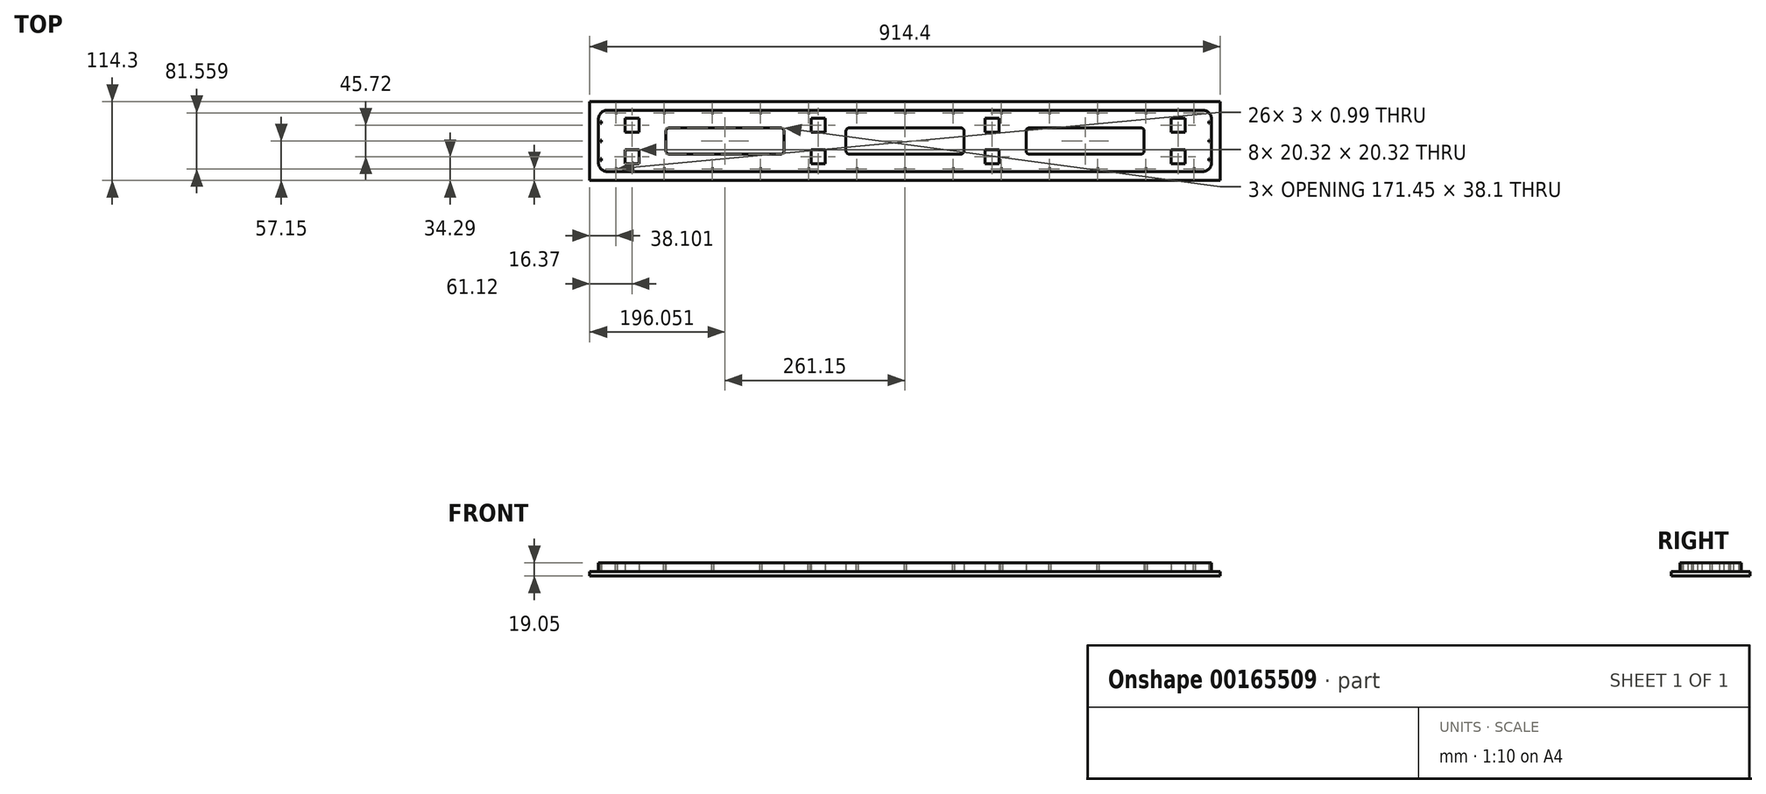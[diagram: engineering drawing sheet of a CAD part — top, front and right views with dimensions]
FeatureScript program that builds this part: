
annotation { "Feature Type Name" : "Feature", "Feature Type Description" : "" }
export const myFeature = defineFeature(function(context is Context, id is Id, definition is map)
    precondition{}
    {
        {
            var Q0;
            Q0=qCreatedBy(makeId("Top.planeOp"),FACE);
            var sketch = newSketch(context, id + "F0", { "sketchPlane" : qUnion([Q0])});
            skLineSegment(sketch, "E0.bottom", {"start": v(0, 33.02) * mm, "end": v(20.32, 33.02) * mm});
            skLineSegment(sketch, "E0.top", {"start": v(0, 12.7) * mm, "end": v(20.32, 12.7) * mm});
            skLineSegment(sketch, "E0.left", {"start": v(0, 33.02) * mm, "end": v(0, 12.7) * mm});
            skLineSegment(sketch, "E0.right", {"start": v(20.32, 33.02) * mm, "end": v(20.32, 12.7) * mm});
            skLineSegment(sketch, "E1.bottom", {"start": v(269.88, 12.7) * mm, "end": v(290.2, 12.7) * mm});
            skLineSegment(sketch, "E1.top", {"start": v(269.88, 33.02) * mm, "end": v(290.2, 33.02) * mm});
            skLineSegment(sketch, "E1.left", {"start": v(269.88, 12.7) * mm, "end": v(269.88, 33.02) * mm});
            skLineSegment(sketch, "E1.right", {"start": v(290.2, 12.7) * mm, "end": v(290.2, 33.02) * mm});
            skLineSegment(sketch, "E2.bottom", {"start": v(522.3, 12.7) * mm, "end": v(542.62, 12.7) * mm});
            skLineSegment(sketch, "E2.top", {"start": v(522.3, 33.02) * mm, "end": v(542.62, 33.02) * mm});
            skLineSegment(sketch, "E2.left", {"start": v(522.3, 12.7) * mm, "end": v(522.3, 33.02) * mm});
            skLineSegment(sketch, "E2.right", {"start": v(542.62, 12.7) * mm, "end": v(542.62, 33.02) * mm});
            skLineSegment(sketch, "E3.bottom", {"start": v(792.16, 12.7) * mm, "end": v(812.48, 12.7) * mm});
            skLineSegment(sketch, "E3.top", {"start": v(792.16, 33.02) * mm, "end": v(812.48, 33.02) * mm});
            skLineSegment(sketch, "E3.left", {"start": v(792.16, 12.7) * mm, "end": v(792.16, 33.02) * mm});
            skLineSegment(sketch, "E3.right", {"start": v(812.48, 12.7) * mm, "end": v(812.48, 33.02) * mm});
            skLineSegment(sketch, "E4.MirrorCS", {"start": v(0, -33.02) * mm, "end": v(0, -12.7) * mm});
            skLineSegment(sketch, "E5.MirrorCS", {"start": v(269.88, -12.7) * mm, "end": v(290.2, -12.7) * mm});
            skLineSegment(sketch, "E6.MirrorCS", {"start": v(0, -33.02) * mm, "end": v(20.32, -33.02) * mm});
            skLineSegment(sketch, "E7.MirrorCS", {"start": v(792.16, -33.02) * mm, "end": v(812.48, -33.02) * mm});
            skLineSegment(sketch, "E8.MirrorCS", {"start": v(792.16, -12.7) * mm, "end": v(792.16, -33.02) * mm});
            skLineSegment(sketch, "E9.MirrorCS", {"start": v(812.48, -12.7) * mm, "end": v(812.48, -33.02) * mm});
            skLineSegment(sketch, "E10.MirrorCS", {"start": v(20.32, -33.02) * mm, "end": v(20.32, -12.7) * mm});
            skLineSegment(sketch, "E11.MirrorCS", {"start": v(269.88, -33.02) * mm, "end": v(290.2, -33.02) * mm});
            skLineSegment(sketch, "E12.MirrorCS", {"start": v(269.88, -12.7) * mm, "end": v(269.88, -33.02) * mm});
            skLineSegment(sketch, "E13.MirrorCS", {"start": v(290.2, -12.7) * mm, "end": v(290.2, -33.02) * mm});
            skLineSegment(sketch, "E14.MirrorCS", {"start": v(522.3, -12.7) * mm, "end": v(542.62, -12.7) * mm});
            skLineSegment(sketch, "E15.MirrorCS", {"start": v(522.3, -33.02) * mm, "end": v(542.62, -33.02) * mm});
            skLineSegment(sketch, "E16.MirrorCS", {"start": v(522.3, -12.7) * mm, "end": v(522.3, -33.02) * mm});
            skLineSegment(sketch, "E17.MirrorCS", {"start": v(542.62, -12.7) * mm, "end": v(542.62, -33.02) * mm});
            skLineSegment(sketch, "E18.MirrorCS", {"start": v(792.16, -12.7) * mm, "end": v(812.48, -12.7) * mm});
            skLineSegment(sketch, "E19.MirrorCS", {"start": v(0, -12.7) * mm, "end": v(20.32, -12.7) * mm});
            skLineSegment(sketch, "E20", {"start": v(0, 0) * mm, "end": v(812.48, 0) * mm, "construction": true});
            skLineSegment(sketch, "E21.bottom", {"start": v(-38.26, -44.45) * mm, "end": v(850.74, -44.45) * mm});
            skLineSegment(sketch, "E21.top", {"start": v(-38.26, 44.45) * mm, "end": v(850.74, 44.45) * mm});
            skLineSegment(sketch, "E21.left", {"start": v(-38.26, -44.45) * mm, "end": v(-38.26, 44.45) * mm});
            skLineSegment(sketch, "E21.right", {"start": v(850.74, -44.45) * mm, "end": v(850.74, 44.45) * mm});
            skPoint(sketch, "E21.middle", {"position": v(406.24, 0) * mm});
            skLineSegment(sketch, "E22.bottom", {"start": v(407.74, 40.28) * mm, "end": v(404.74, 40.28) * mm});
            skLineSegment(sketch, "E22.top", {"start": v(407.74, 41.28) * mm, "end": v(404.74, 41.28) * mm});
            skLineSegment(sketch, "E22.left", {"start": v(407.74, 40.28) * mm, "end": v(407.74, 41.28) * mm});
            skLineSegment(sketch, "E22.right", {"start": v(404.74, 40.28) * mm, "end": v(404.74, 41.28) * mm});
            skPoint(sketch, "E22.middle", {"position": v(406.24, 40.78) * mm});
            skLineSegment(sketch, "E23.1.0.0", {"start": v(477.59, 41.28) * mm, "end": v(474.6, 41.28) * mm});
            skLineSegment(sketch, "E23.1.0.1", {"start": v(474.6, 40.28) * mm, "end": v(474.6, 41.28) * mm});
            skLineSegment(sketch, "E23.1.0.2", {"start": v(477.59, 40.28) * mm, "end": v(474.6, 40.28) * mm});
            skLineSegment(sketch, "E23.1.0.3", {"start": v(477.59, 40.28) * mm, "end": v(477.59, 41.28) * mm});
            skLineSegment(sketch, "E23.2.0.0", {"start": v(547.44, 41.28) * mm, "end": v(544.44, 41.28) * mm});
            skLineSegment(sketch, "E23.2.0.1", {"start": v(544.44, 40.28) * mm, "end": v(544.44, 41.28) * mm});
            skLineSegment(sketch, "E23.2.0.2", {"start": v(547.44, 40.28) * mm, "end": v(544.44, 40.28) * mm});
            skLineSegment(sketch, "E23.2.0.3", {"start": v(547.44, 40.28) * mm, "end": v(547.44, 41.28) * mm});
            skLineSegment(sketch, "E23.3.0.0", {"start": v(617.29, 41.28) * mm, "end": v(614.3, 41.28) * mm});
            skLineSegment(sketch, "E23.3.0.1", {"start": v(614.3, 40.28) * mm, "end": v(614.3, 41.28) * mm});
            skLineSegment(sketch, "E23.3.0.2", {"start": v(617.29, 40.28) * mm, "end": v(614.3, 40.28) * mm});
            skLineSegment(sketch, "E23.3.0.3", {"start": v(617.29, 40.28) * mm, "end": v(617.29, 41.28) * mm});
            skLineSegment(sketch, "E23.4.0.0", {"start": v(687.14, 41.28) * mm, "end": v(684.14, 41.28) * mm});
            skLineSegment(sketch, "E23.4.0.1", {"start": v(684.14, 40.28) * mm, "end": v(684.14, 41.28) * mm});
            skLineSegment(sketch, "E23.4.0.2", {"start": v(687.14, 40.28) * mm, "end": v(684.14, 40.28) * mm});
            skLineSegment(sketch, "E23.4.0.3", {"start": v(687.14, 40.28) * mm, "end": v(687.14, 41.28) * mm});
            skLineSegment(sketch, "E23.5.0.0", {"start": v(756.99, 41.28) * mm, "end": v(754, 41.28) * mm});
            skLineSegment(sketch, "E23.5.0.1", {"start": v(754, 40.28) * mm, "end": v(754, 41.28) * mm});
            skLineSegment(sketch, "E23.5.0.2", {"start": v(756.99, 40.28) * mm, "end": v(754, 40.28) * mm});
            skLineSegment(sketch, "E23.5.0.3", {"start": v(756.99, 40.28) * mm, "end": v(756.99, 41.28) * mm});
            skLineSegment(sketch, "E23.6.0.0", {"start": v(826.84, 41.28) * mm, "end": v(823.84, 41.28) * mm});
            skLineSegment(sketch, "E23.6.0.1", {"start": v(823.84, 40.28) * mm, "end": v(823.84, 41.28) * mm});
            skLineSegment(sketch, "E23.6.0.2", {"start": v(826.84, 40.28) * mm, "end": v(823.84, 40.28) * mm});
            skLineSegment(sketch, "E23.6.0.3", {"start": v(826.84, 40.28) * mm, "end": v(826.84, 41.28) * mm});
            skLineSegment(sketch, "E23.direction1", {"start": v(404.74, 41.28) * mm, "end": v(474.6, 41.28) * mm, "construction": true});
            skLineSegment(sketch, "E24", {"start": v(406.24, 44.45) * mm, "end": v(406.24, -44.45) * mm, "construction": true});
            skLineSegment(sketch, "E25.MirrorCS", {"start": v(58.49, 40.28) * mm, "end": v(58.49, 41.28) * mm});
            skLineSegment(sketch, "E26.MirrorCS", {"start": v(337.89, 40.28) * mm, "end": v(337.89, 41.28) * mm});
            skLineSegment(sketch, "E27.MirrorCS", {"start": v(334.9, 40.28) * mm, "end": v(337.89, 40.28) * mm});
            skLineSegment(sketch, "E28.MirrorCS", {"start": v(195.2, 40.28) * mm, "end": v(198.19, 40.28) * mm});
            skLineSegment(sketch, "E29.MirrorCS", {"start": v(55.5, 40.28) * mm, "end": v(58.49, 40.28) * mm});
            skLineSegment(sketch, "E30.MirrorCS", {"start": v(-14.36, 41.28) * mm, "end": v(-11.36, 41.28) * mm});
            skLineSegment(sketch, "E31.MirrorCS", {"start": v(195.2, 40.28) * mm, "end": v(195.2, 41.28) * mm});
            skLineSegment(sketch, "E32.MirrorCS", {"start": v(265.04, 41.28) * mm, "end": v(268.04, 41.28) * mm});
            skLineSegment(sketch, "E33.MirrorCS", {"start": v(55.5, 40.28) * mm, "end": v(55.5, 41.28) * mm});
            skLineSegment(sketch, "E34.MirrorCS", {"start": v(334.9, 40.28) * mm, "end": v(334.9, 41.28) * mm});
            skLineSegment(sketch, "E35.MirrorCS", {"start": v(-11.36, 40.28) * mm, "end": v(-11.36, 41.28) * mm});
            skLineSegment(sketch, "E36.MirrorCS", {"start": v(125.34, 41.28) * mm, "end": v(128.34, 41.28) * mm});
            skLineSegment(sketch, "E37.MirrorCS", {"start": v(268.04, 40.28) * mm, "end": v(268.04, 41.28) * mm});
            skLineSegment(sketch, "E38.MirrorCS", {"start": v(-14.36, 40.28) * mm, "end": v(-11.36, 40.28) * mm});
            skLineSegment(sketch, "E39.MirrorCS", {"start": v(265.04, 40.28) * mm, "end": v(268.04, 40.28) * mm});
            skLineSegment(sketch, "E40.MirrorCS", {"start": v(128.34, 40.28) * mm, "end": v(128.34, 41.28) * mm});
            skLineSegment(sketch, "E41.MirrorCS", {"start": v(125.34, 40.28) * mm, "end": v(128.34, 40.28) * mm});
            skLineSegment(sketch, "E42.MirrorCS", {"start": v(-14.36, 40.28) * mm, "end": v(-14.36, 41.28) * mm});
            skLineSegment(sketch, "E43.MirrorCS", {"start": v(265.04, 40.28) * mm, "end": v(265.04, 41.28) * mm});
            skLineSegment(sketch, "E44.MirrorCS", {"start": v(125.34, 40.28) * mm, "end": v(125.34, 41.28) * mm});
            skLineSegment(sketch, "E45.MirrorCS", {"start": v(195.2, 41.28) * mm, "end": v(198.19, 41.28) * mm});
            skLineSegment(sketch, "E46.MirrorCS", {"start": v(55.5, 41.28) * mm, "end": v(58.49, 41.28) * mm});
            skLineSegment(sketch, "E47.MirrorCS", {"start": v(334.9, 41.28) * mm, "end": v(337.89, 41.28) * mm});
            skLineSegment(sketch, "E48.MirrorCS", {"start": v(198.19, 40.28) * mm, "end": v(198.19, 41.28) * mm});
            skLineSegment(sketch, "E49.MirrorCS", {"start": v(404.74, -40.28) * mm, "end": v(404.74, -41.28) * mm});
            skLineSegment(sketch, "E50.MirrorCS", {"start": v(407.74, -40.28) * mm, "end": v(407.74, -41.28) * mm});
            skLineSegment(sketch, "E51.MirrorCS", {"start": v(407.74, -40.28) * mm, "end": v(404.74, -40.28) * mm});
            skLineSegment(sketch, "E52.MirrorCS", {"start": v(407.74, -41.28) * mm, "end": v(404.74, -41.28) * mm});
            skLineSegment(sketch, "E53.MirrorCS", {"start": v(477.59, -40.28) * mm, "end": v(477.59, -41.28) * mm});
            skLineSegment(sketch, "E54.MirrorCS", {"start": v(477.59, -40.28) * mm, "end": v(474.6, -40.28) * mm});
            skLineSegment(sketch, "E55.MirrorCS", {"start": v(474.6, -40.28) * mm, "end": v(474.6, -41.28) * mm});
            skLineSegment(sketch, "E56.MirrorCS", {"start": v(477.59, -41.28) * mm, "end": v(474.6, -41.28) * mm});
            skLineSegment(sketch, "E57.MirrorCS", {"start": v(58.49, -40.28) * mm, "end": v(58.49, -41.28) * mm});
            skLineSegment(sketch, "E58.MirrorCS", {"start": v(-14.36, -40.28) * mm, "end": v(-14.36, -41.28) * mm});
            skLineSegment(sketch, "E59.MirrorCS", {"start": v(128.34, -40.28) * mm, "end": v(128.34, -41.28) * mm});
            skLineSegment(sketch, "E60.MirrorCS", {"start": v(265.04, -40.28) * mm, "end": v(268.04, -40.28) * mm});
            skLineSegment(sketch, "E61.MirrorCS", {"start": v(-14.36, -40.28) * mm, "end": v(-11.36, -40.28) * mm});
            skLineSegment(sketch, "E62.MirrorCS", {"start": v(268.04, -40.28) * mm, "end": v(268.04, -41.28) * mm});
            skLineSegment(sketch, "E63.MirrorCS", {"start": v(125.34, -41.28) * mm, "end": v(128.34, -41.28) * mm});
            skLineSegment(sketch, "E64.MirrorCS", {"start": v(334.9, -40.28) * mm, "end": v(334.9, -41.28) * mm});
            skLineSegment(sketch, "E65.MirrorCS", {"start": v(-11.36, -40.28) * mm, "end": v(-11.36, -41.28) * mm});
            skLineSegment(sketch, "E66.MirrorCS", {"start": v(55.5, -40.28) * mm, "end": v(55.5, -41.28) * mm});
            skLineSegment(sketch, "E67.MirrorCS", {"start": v(265.04, -41.28) * mm, "end": v(268.04, -41.28) * mm});
            skLineSegment(sketch, "E68.MirrorCS", {"start": v(198.19, -40.28) * mm, "end": v(198.19, -41.28) * mm});
            skLineSegment(sketch, "E69.MirrorCS", {"start": v(195.2, -40.28) * mm, "end": v(195.2, -41.28) * mm});
            skLineSegment(sketch, "E70.MirrorCS", {"start": v(334.9, -41.28) * mm, "end": v(337.89, -41.28) * mm});
            skLineSegment(sketch, "E71.MirrorCS", {"start": v(-14.36, -41.28) * mm, "end": v(-11.36, -41.28) * mm});
            skLineSegment(sketch, "E72.MirrorCS", {"start": v(55.5, -41.28) * mm, "end": v(58.49, -41.28) * mm});
            skLineSegment(sketch, "E73.MirrorCS", {"start": v(55.5, -40.28) * mm, "end": v(58.49, -40.28) * mm});
            skLineSegment(sketch, "E74.MirrorCS", {"start": v(195.2, -41.28) * mm, "end": v(198.19, -41.28) * mm});
            skLineSegment(sketch, "E75.MirrorCS", {"start": v(125.34, -40.28) * mm, "end": v(125.34, -41.28) * mm});
            skLineSegment(sketch, "E76.MirrorCS", {"start": v(334.9, -40.28) * mm, "end": v(337.89, -40.28) * mm});
            skLineSegment(sketch, "E77.MirrorCS", {"start": v(195.2, -40.28) * mm, "end": v(198.19, -40.28) * mm});
            skLineSegment(sketch, "E78.MirrorCS", {"start": v(337.89, -40.28) * mm, "end": v(337.89, -41.28) * mm});
            skLineSegment(sketch, "E79.MirrorCS", {"start": v(125.34, -40.28) * mm, "end": v(128.34, -40.28) * mm});
            skLineSegment(sketch, "E80.MirrorCS", {"start": v(265.04, -40.28) * mm, "end": v(265.04, -41.28) * mm});
            skLineSegment(sketch, "E81.MirrorCS", {"start": v(404.74, -41.28) * mm, "end": v(474.6, -41.28) * mm, "construction": true});
            skPoint(sketch, "E82.MirrorP", {"position": v(406.24, -40.78) * mm});
            skLineSegment(sketch, "E83.MirrorCS", {"start": v(617.29, -40.28) * mm, "end": v(614.3, -40.28) * mm});
            skLineSegment(sketch, "E84.MirrorCS", {"start": v(617.29, -40.28) * mm, "end": v(617.29, -41.28) * mm});
            skLineSegment(sketch, "E85.MirrorCS", {"start": v(687.14, -41.28) * mm, "end": v(684.14, -41.28) * mm});
            skLineSegment(sketch, "E86.MirrorCS", {"start": v(684.14, -40.28) * mm, "end": v(684.14, -41.28) * mm});
            skLineSegment(sketch, "E87.MirrorCS", {"start": v(687.14, -40.28) * mm, "end": v(684.14, -40.28) * mm});
            skLineSegment(sketch, "E88.MirrorCS", {"start": v(687.14, -40.28) * mm, "end": v(687.14, -41.28) * mm});
            skLineSegment(sketch, "E89.MirrorCS", {"start": v(756.99, -41.28) * mm, "end": v(754, -41.28) * mm});
            skLineSegment(sketch, "E90.MirrorCS", {"start": v(754, -40.28) * mm, "end": v(754, -41.28) * mm});
            skLineSegment(sketch, "E91.MirrorCS", {"start": v(756.99, -40.28) * mm, "end": v(754, -40.28) * mm});
            skLineSegment(sketch, "E92.MirrorCS", {"start": v(826.84, -41.28) * mm, "end": v(823.84, -41.28) * mm});
            skLineSegment(sketch, "E93.MirrorCS", {"start": v(547.44, -41.28) * mm, "end": v(544.44, -41.28) * mm});
            skLineSegment(sketch, "E94.MirrorCS", {"start": v(614.3, -40.28) * mm, "end": v(614.3, -41.28) * mm});
            skLineSegment(sketch, "E95.MirrorCS", {"start": v(547.44, -40.28) * mm, "end": v(547.44, -41.28) * mm});
            skLineSegment(sketch, "E96.MirrorCS", {"start": v(826.84, -40.28) * mm, "end": v(826.84, -41.28) * mm});
            skLineSegment(sketch, "E97.MirrorCS", {"start": v(756.99, -40.28) * mm, "end": v(756.99, -41.28) * mm});
            skLineSegment(sketch, "E98.MirrorCS", {"start": v(823.84, -40.28) * mm, "end": v(823.84, -41.28) * mm});
            skLineSegment(sketch, "E99.MirrorCS", {"start": v(826.84, -40.28) * mm, "end": v(823.84, -40.28) * mm});
            skLineSegment(sketch, "E100.MirrorCS", {"start": v(617.29, -41.28) * mm, "end": v(614.3, -41.28) * mm});
            skLineSegment(sketch, "E101.MirrorCS", {"start": v(547.44, -40.28) * mm, "end": v(544.44, -40.28) * mm});
            skLineSegment(sketch, "E102.MirrorCS", {"start": v(544.44, -40.28) * mm, "end": v(544.44, -41.28) * mm});
            skLineSegment(sketch, "E103.bottom", {"start": v(847.57, -1.5) * mm, "end": v(846.58, -1.5) * mm});
            skLineSegment(sketch, "E103.top", {"start": v(847.57, 1.5) * mm, "end": v(846.58, 1.5) * mm});
            skLineSegment(sketch, "E103.left", {"start": v(847.57, -1.5) * mm, "end": v(847.57, 1.5) * mm});
            skLineSegment(sketch, "E103.right", {"start": v(846.58, -1.5) * mm, "end": v(846.58, 1.5) * mm});
            skPoint(sketch, "E103.middle", {"position": v(847.07, 0) * mm});
            skLineSegment(sketch, "E104.bottom", {"start": v(847.57, 25.49) * mm, "end": v(846.58, 25.49) * mm});
            skLineSegment(sketch, "E104.top", {"start": v(847.57, 28.49) * mm, "end": v(846.58, 28.49) * mm});
            skLineSegment(sketch, "E104.left", {"start": v(847.57, 25.49) * mm, "end": v(847.57, 28.49) * mm});
            skLineSegment(sketch, "E104.right", {"start": v(846.58, 25.49) * mm, "end": v(846.58, 28.49) * mm});
            skPoint(sketch, "E104.middle", {"position": v(847.07, 26.99) * mm});
            skLineSegment(sketch, "E105.MirrorCS", {"start": v(847.57, -28.49) * mm, "end": v(846.58, -28.49) * mm});
            skLineSegment(sketch, "E106.MirrorCS", {"start": v(847.57, -25.49) * mm, "end": v(846.58, -25.49) * mm});
            skLineSegment(sketch, "E107.MirrorCS", {"start": v(846.58, -25.49) * mm, "end": v(846.58, -28.49) * mm});
            skLineSegment(sketch, "E108.MirrorCS", {"start": v(847.57, -25.49) * mm, "end": v(847.57, -28.49) * mm});
            skPoint(sketch, "E109.MirrorP", {"position": v(847.07, -26.99) * mm});
            skLineSegment(sketch, "E110.MirrorCS", {"start": v(-35.08, 25.49) * mm, "end": v(-34.1, 25.49) * mm});
            skLineSegment(sketch, "E111.MirrorCS", {"start": v(-35.08, 28.49) * mm, "end": v(-34.1, 28.49) * mm});
            skLineSegment(sketch, "E112.MirrorCS", {"start": v(-35.08, -28.49) * mm, "end": v(-34.1, -28.49) * mm});
            skLineSegment(sketch, "E113.MirrorCS", {"start": v(-35.08, -25.49) * mm, "end": v(-34.1, -25.49) * mm});
            skLineSegment(sketch, "E114.MirrorCS", {"start": v(-35.08, -1.5) * mm, "end": v(-34.1, -1.5) * mm});
            skLineSegment(sketch, "E115.MirrorCS", {"start": v(-35.08, 1.5) * mm, "end": v(-34.1, 1.5) * mm});
            skLineSegment(sketch, "E116.MirrorCS", {"start": v(-34.1, -1.5) * mm, "end": v(-34.1, 1.5) * mm});
            skLineSegment(sketch, "E117.MirrorCS", {"start": v(-35.08, 25.49) * mm, "end": v(-35.08, 28.49) * mm});
            skLineSegment(sketch, "E118.MirrorCS", {"start": v(-34.1, 25.49) * mm, "end": v(-34.1, 28.49) * mm});
            skLineSegment(sketch, "E119.MirrorCS", {"start": v(-34.1, -25.49) * mm, "end": v(-34.1, -28.49) * mm});
            skLineSegment(sketch, "E120.MirrorCS", {"start": v(-35.08, -25.49) * mm, "end": v(-35.08, -28.49) * mm});
            skLineSegment(sketch, "E121.MirrorCS", {"start": v(-35.08, -1.5) * mm, "end": v(-35.08, 1.5) * mm});
            skPoint(sketch, "E122.MirrorP", {"position": v(-34.59, -26.99) * mm});
            skPoint(sketch, "E123.MirrorP", {"position": v(-34.59, 0) * mm});
            skPoint(sketch, "E124.MirrorP", {"position": v(-34.59, 26.99) * mm});
            skLineSegment(sketch, "E125.bottom", {"start": v(491.97, -19.05) * mm, "end": v(320.52, -19.05) * mm});
            skLineSegment(sketch, "E125.top", {"start": v(491.97, 19.05) * mm, "end": v(320.52, 19.05) * mm});
            skLineSegment(sketch, "E125.left", {"start": v(491.97, -19.05) * mm, "end": v(491.97, 19.05) * mm});
            skLineSegment(sketch, "E125.right", {"start": v(320.52, -19.05) * mm, "end": v(320.52, 19.05) * mm});
            skLineSegment(sketch, "E126", {"start": v(542.62, 12.7) * mm, "end": v(792.16, 12.7) * mm, "construction": true});
            skLineSegment(sketch, "E127.bottom", {"start": v(753.12, -19.05) * mm, "end": v(581.67, -19.05) * mm});
            skLineSegment(sketch, "E127.top", {"start": v(753.12, 19.05) * mm, "end": v(581.67, 19.05) * mm});
            skLineSegment(sketch, "E127.left", {"start": v(753.12, -19.05) * mm, "end": v(753.12, 19.05) * mm});
            skLineSegment(sketch, "E127.right", {"start": v(581.67, -19.05) * mm, "end": v(581.67, 19.05) * mm});
            skPoint(sketch, "E127.middle", {"position": v(667.4, 0) * mm});
            skPoint(sketch, "E127.middle.positionSnap0", {"position": v(667.4, 12.7) * mm});
            skPoint(sketch, "E127.centerSnap0", {"position": v(667.4, 12.7) * mm});
            skPoint(sketch, "E128.MirrorP", {"position": v(145.1, 12.7) * mm});
            skLineSegment(sketch, "E129.MirrorCS", {"start": v(59.37, 19.05) * mm, "end": v(230.82, 19.05) * mm});
            skPoint(sketch, "E130.MirrorP", {"position": v(145.1, 0) * mm});
            skLineSegment(sketch, "E131.MirrorCS", {"start": v(230.82, -19.05) * mm, "end": v(230.82, 19.05) * mm});
            skLineSegment(sketch, "E132.MirrorCS", {"start": v(59.37, -19.05) * mm, "end": v(230.82, -19.05) * mm});
            skLineSegment(sketch, "E133.MirrorCS", {"start": v(59.37, -19.05) * mm, "end": v(59.37, 19.05) * mm});
            skLineSegment(sketch, "E134.bottom", {"start": v(863.44, -57.15) * mm, "end": v(-50.96, -57.15) * mm, "construction": true});
            skLineSegment(sketch, "E134.top", {"start": v(863.44, 57.15) * mm, "end": v(-50.96, 57.15) * mm, "construction": true});
            skLineSegment(sketch, "E134.left", {"start": v(863.44, -57.15) * mm, "end": v(863.44, 57.15) * mm, "construction": true});
            skLineSegment(sketch, "E134.right", {"start": v(-50.96, -57.15) * mm, "end": v(-50.96, 57.15) * mm, "construction": true});
            skSolve(sketch);
        }
        {
            var Q0;
            Q0=qSketchRegion(id+"F0",true);
            extrude(context, id + "F1", {"entities" : qUnion([Q0]), "depth" : 12.7 * mm});
        }
        {
            var Q0;
            Q0=makeQuery(id+"F1.opExtrude","SWEPT_EDGE",EDGE,{"disambiguationData":[OSD([sQuery(id+"F0.wireOp",EDGE,"E21.top"),sQuery(id+"F0.wireOp",EDGE,"E21.right")])]});
            var Q1;
            Q1=makeQuery(id+"F1.opExtrude","SWEPT_EDGE",EDGE,{"disambiguationData":[OSD([sQuery(id+"F0.wireOp",EDGE,"E21.bottom"),sQuery(id+"F0.wireOp",EDGE,"E21.right")])]});
            var Q2;
            Q2=makeQuery(id+"F1.opExtrude","SWEPT_EDGE",EDGE,{"disambiguationData":[OSD([sQuery(id+"F0.wireOp",EDGE,"E21.top"),sQuery(id+"F0.wireOp",EDGE,"E21.left")])]});
            var Q3;
            Q3=makeQuery(id+"F1.opExtrude","SWEPT_EDGE",EDGE,{"disambiguationData":[OSD([sQuery(id+"F0.wireOp",EDGE,"E21.bottom"),sQuery(id+"F0.wireOp",EDGE,"E21.left")])]});
            fillet(context, id + "F2", {"entities" : qUnion([Q0, Q1, Q2, Q3]), "radius" : 12.7 * mm, "tangentPropagation" : true, "allowEdgeOverflow" : false});
        }
        {
            var Q0;
            Q0=makeQuery(id+"F1.opExtrude","SWEPT_EDGE",EDGE,{"disambiguationData":[OSD([sQuery(id+"F0.wireOp",EDGE,"E129.MirrorCS"),sQuery(id+"F0.wireOp",EDGE,"E133.MirrorCS")])]});
            var Q1;
            Q1=makeQuery(id+"F1.opExtrude","SWEPT_EDGE",EDGE,{"disambiguationData":[OSD([sQuery(id+"F0.wireOp",EDGE,"E125.top"),sQuery(id+"F0.wireOp",EDGE,"E125.right")])]});
            var Q2;
            Q2=makeQuery(id+"F1.opExtrude","SWEPT_EDGE",EDGE,{"disambiguationData":[OSD([sQuery(id+"F0.wireOp",EDGE,"E127.top"),sQuery(id+"F0.wireOp",EDGE,"E127.right")])]});
            var Q3;
            Q3=makeQuery(id+"F1.opExtrude","SWEPT_EDGE",EDGE,{"disambiguationData":[OSD([sQuery(id+"F0.wireOp",EDGE,"E127.top"),sQuery(id+"F0.wireOp",EDGE,"E127.left")])]});
            var Q4;
            Q4=makeQuery(id+"F1.opExtrude","SWEPT_EDGE",EDGE,{"disambiguationData":[OSD([sQuery(id+"F0.wireOp",EDGE,"E125.top"),sQuery(id+"F0.wireOp",EDGE,"E125.left")])]});
            var Q5;
            Q5=makeQuery(id+"F1.opExtrude","SWEPT_EDGE",EDGE,{"disambiguationData":[OSD([sQuery(id+"F0.wireOp",EDGE,"E129.MirrorCS"),sQuery(id+"F0.wireOp",EDGE,"E131.MirrorCS")])]});
            var Q6;
            Q6=makeQuery(id+"F1.opExtrude","SWEPT_EDGE",EDGE,{"disambiguationData":[OSD([sQuery(id+"F0.wireOp",EDGE,"E131.MirrorCS"),sQuery(id+"F0.wireOp",EDGE,"E132.MirrorCS")])]});
            var Q7;
            Q7=makeQuery(id+"F1.opExtrude","SWEPT_EDGE",EDGE,{"disambiguationData":[OSD([sQuery(id+"F0.wireOp",EDGE,"E125.bottom"),sQuery(id+"F0.wireOp",EDGE,"E125.left")])]});
            var Q8;
            Q8=makeQuery(id+"F1.opExtrude","SWEPT_EDGE",EDGE,{"disambiguationData":[OSD([sQuery(id+"F0.wireOp",EDGE,"E127.bottom"),sQuery(id+"F0.wireOp",EDGE,"E127.left")])]});
            var Q9;
            Q9=makeQuery(id+"F1.opExtrude","SWEPT_EDGE",EDGE,{"disambiguationData":[OSD([sQuery(id+"F0.wireOp",EDGE,"E127.bottom"),sQuery(id+"F0.wireOp",EDGE,"E127.right")])]});
            var Q10;
            Q10=makeQuery(id+"F1.opExtrude","SWEPT_EDGE",EDGE,{"disambiguationData":[OSD([sQuery(id+"F0.wireOp",EDGE,"E125.bottom"),sQuery(id+"F0.wireOp",EDGE,"E125.right")])]});
            var Q11;
            Q11=makeQuery(id+"F1.opExtrude","SWEPT_EDGE",EDGE,{"disambiguationData":[OSD([sQuery(id+"F0.wireOp",EDGE,"E132.MirrorCS"),sQuery(id+"F0.wireOp",EDGE,"E133.MirrorCS")])]});
            fillet(context, id + "F3", {"entities" : qUnion([Q0, Q1, Q2, Q3, Q4, Q5, Q6, Q7, Q8, Q9, Q10, Q11]), "radius" : 5.08 * mm, "tangentPropagation" : true, "allowEdgeOverflow" : false});
        }
        {
            var Q0;
            Q0=makeQuery(id+"F1.opExtrude","CAP_FACE",FACE,{"disambiguationData":[OSD([sQuery(id+"F0.wireOp",EDGE,"E21.bottom"),sQuery(id+"F0.wireOp",EDGE,"E21.top"),sQuery(id+"F0.wireOp",EDGE,"E21.left"),sQuery(id+"F0.wireOp",EDGE,"E21.right"),sQuery(id+"F0.wireOp",EDGE,"E134.bottom"),sQuery(id+"F0.wireOp",EDGE,"E134.top"),sQuery(id+"F0.wireOp",EDGE,"E134.left"),sQuery(id+"F0.wireOp",EDGE,"E134.right")])],"isStart":true});
            var sketch = newSketch(context, id + "F4", { "sketchPlane" : qUnion([Q0])});
            skLineSegment(sketch, "E135.0", {"start": v(863.44, 57.15) * mm, "end": v(-50.96, 57.15) * mm});
            skLineSegment(sketch, "E135.1", {"start": v(-50.96, 57.15) * mm, "end": v(-50.96, -57.15) * mm});
            skLineSegment(sketch, "E135.2", {"start": v(863.44, -57.15) * mm, "end": v(-50.96, -57.15) * mm});
            skLineSegment(sketch, "E135.3", {"start": v(863.44, 57.15) * mm, "end": v(863.44, -57.15) * mm});
            skSolve(sketch);
        }
        {
            var Q0;
            Q0=qSketchRegion(id+"F4",true);
            extrude(context, id + "F5", {"entities" : qUnion([Q0]), "depth" : 6.35 * mm});
        }
    });
